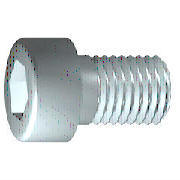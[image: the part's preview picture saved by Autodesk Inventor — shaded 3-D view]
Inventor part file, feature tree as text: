
AUTODESK INVENTOR PART (.ipt)
format: ipt  version: 2022 (Build 260153000, 153)  size: 196,096 bytes
history: native  units: mm (DEFAULTED — no unit token found)
features: sketch x2, other x1, extrude x1, plane x1, fillet x1
ambient origin geometry x7: Origin, YZ Plane, XY Plane, X Axis, Y Axis, Z Axis, Center Point
bodies: Solid1 (feature_tree)
feature tree (6):
  other  "Базовый элемент"
  extrude  "Паз"  Depth=9.9mm
  plane  "Work Plane1"
  fillet  "Fillet2"  Radius=0.429515mm
  sketch  "Эскиз1"
  sketch  "Эскиз2"
